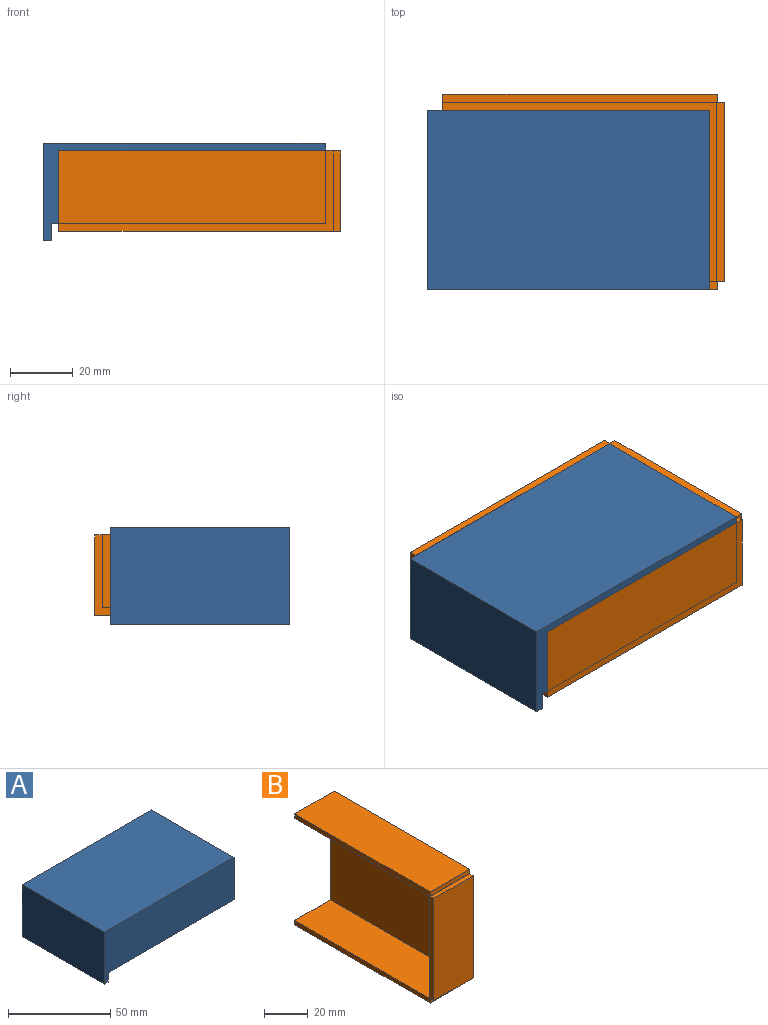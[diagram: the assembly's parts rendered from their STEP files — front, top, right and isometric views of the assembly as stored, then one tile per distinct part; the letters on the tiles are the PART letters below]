
ASSEMBLY  parts=2 mates=1
PART A: 13 faces, bbox 89.8x57.1x31.1 mm
  f0: plane 87.3x57.1mm, normal (0,0,-1), area 697mm2, adj f1,f2,f3,f5,f6,f7,f8,f10
  f1: plane 89.8x31.12mm, normal (0,1,0), area 2304mm2, adj f0,f3,f4,f10,f11,f12
  f2: plane 89.8x31.12mm, normal (0,-1,0), area 2304mm2, adj f0,f3,f4,f10,f11,f12
  f3: plane 57.1x25.5mm, normal (1,0,0), area 1456mm2, adj f0,f1,f2,f4
  f4: plane 89.8x57.1mm, normal (0,0,1), area 5127.6mm2, adj f1,f2,f3,f12
  f5: plane 82.3x23mm, normal (0,-1,0), area 1892.9mm2, adj f0,f6,f8,f9
  f6: plane 52.1x23mm, normal (1,0,0), area 1198.3mm2, adj f0,f5,f7,f9
  f7: plane 82.3x23mm, normal (0,1,0), area 1892.9mm2, adj f0,f6,f8,f9
  f8: plane 52.1x23mm, normal (-1,0,0), area 1198.3mm2, adj f0,f5,f7,f9
  f9: plane 82.3x52.1mm, normal (0,0,-1), area 4287.8mm2, adj f5,f6,f7,f8
  f10: plane 57.1x5.62mm, normal (1,0,0), area 320.9mm2, adj f0,f1,f2,f11
  f11: plane 57.1x2.5mm, normal (0,0,-1), area 142.7mm2, adj f1,f2,f10,f12
  f12: plane 57.1x31.12mm, normal (-1,0,0), area 1777mm2, adj f1,f2,f4,f11
PART B: 14 faces, bbox 25.5x89.8x62.1 mm
  f0: plane 62.11x25.5mm, normal (0,1,0), area 270.3mm2, adj f1,f2,f3,f5,f6,f12,f13
  f1: plane 89.81x62.11mm, normal (1,0,0), area 5566.3mm2, adj f0,f6,f7,f8,f9,f10,f11,f12
  f2: plane 87.31x57.11mm, normal (-1,0,0), area 4986.3mm2, adj f0,f3,f4,f5
  f3: plane 87.31x23mm, normal (0,0,-1), area 2008.1mm2, adj f0,f2,f4,f13
  f4: plane 57.11x23mm, normal (0,1,0), area 1313.5mm2, adj f2,f3,f5,f13
  f5: plane 87.31x23mm, normal (0,0,1), area 2008.1mm2, adj f0,f2,f4,f13
  f6: plane 87.45x25.5mm, normal (0,0,1), area 2230mm2, adj f0,f1,f7,f13
  f7: plane 25.5x2.5mm, normal (0,-1,0), area 63.7mm2, adj f1,f6,f8,f13
  f8: plane 25.5x2.36mm, normal (0,0,1), area 60.2mm2, adj f1,f7,f9,f13
  f9: plane 57.11x25.5mm, normal (0,-1,0), area 1456.3mm2, adj f1,f8,f10,f13
  f10: plane 25.5x2.36mm, normal (0,0,-1), area 60.2mm2, adj f1,f9,f11,f13
  f11: plane 25.5x2.5mm, normal (0,-1,0), area 63.7mm2, adj f1,f10,f12,f13
  f12: plane 87.45x25.5mm, normal (0,0,-1), area 2230mm2, adj f0,f1,f11,f13
  f13: plane 89.81x62.11mm, normal (-1,0,0), area 580mm2, adj f0,f3,f4,f5,f6,f7,f8,f9
PLACE A t=(-6.64,0.72,-8.92)mm
PLACE B rot(axis=(-0.58,0.58,0.58),120deg) t=(0.27,9.8,-8.92)mm
MATE fastened B.f2 <-> A.f0  axis (0,0,1) through (-55,-23.29,-8.92)mm
